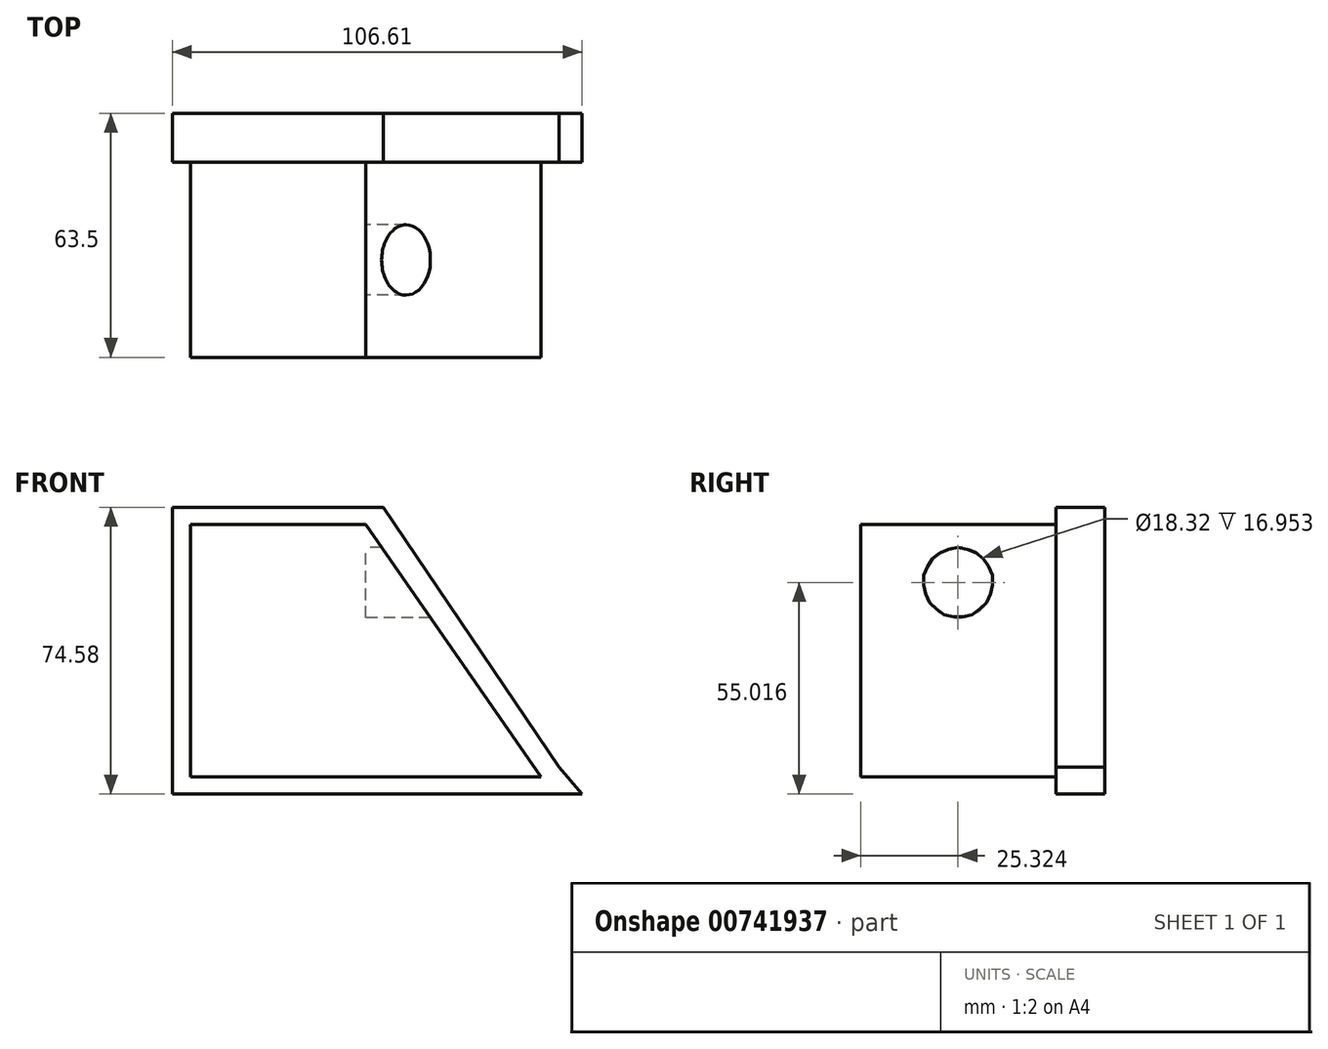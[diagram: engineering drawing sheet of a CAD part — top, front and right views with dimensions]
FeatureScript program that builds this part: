
annotation { "Feature Type Name" : "Feature", "Feature Type Description" : "" }
export const myFeature = defineFeature(function(context is Context, id is Id, definition is map)
    precondition{}
    {
        {
            var Q0;
            Q0=qCreatedBy(makeId("Front.planeOp"),FACE);
            var sketch = newSketch(context, id + "F0", { "sketchPlane" : qUnion([Q0])});
            skLineSegment(sketch, "E0.bottom", {"start": v(45.65, -32.81) * mm, "end": v(-45.65, -32.81) * mm});
            skLineSegment(sketch, "E0.top", {"start": v(0, 32.81) * mm, "end": v(-45.65, 32.81) * mm});
            skLineSegment(sketch, "E0.right", {"start": v(-45.65, -32.81) * mm, "end": v(-45.65, 32.81) * mm});
            skPoint(sketch, "E0.middle", {"position": v(0, 0) * mm});
            skLineSegment(sketch, "E1", {"start": v(45.65, -32.81) * mm, "end": v(0, 32.81) * mm});
            skPoint(sketch, "E0.left.end.orphan", {"position": v(45.65, 32.81) * mm});
            skSolve(sketch);
        }
        {
            var Q0;
            Q0=qCreatedBy(makeId("Front.planeOp"),FACE);
            var sketch = newSketch(context, id + "F1", { "sketchPlane" : qUnion([Q0])});
            skLineSegment(sketch, "E2.bottom", {"start": v(-50.31, 37.29) * mm, "end": v(4.53, 37.29) * mm});
            skLineSegment(sketch, "E2.top", {"start": v(-50.31, -37.29) * mm, "end": v(50.31, -37.29) * mm});
            skLineSegment(sketch, "E2.left", {"start": v(-50.31, 37.29) * mm, "end": v(-50.31, -37.29) * mm});
            skPoint(sketch, "E2.middle", {"position": v(0, 0) * mm});
            skLineSegment(sketch, "E3", {"start": v(50.31, -30.28) * mm, "end": v(4.53, 37.29) * mm});
            skPoint(sketch, "E4.orphan", {"position": v(50.31, 37.29) * mm});
            skLineSegment(sketch, "E5", {"start": v(50.31, -30.28) * mm, "end": v(56.3, -37.29) * mm});
            skLineSegment(sketch, "E6", {"start": v(56.3, -37.29) * mm, "end": v(50.31, -37.29) * mm});
            skSolve(sketch);
        }
        {
            var Q0;
            Q0=makeQuery(id+"F0.imprint","IMPRINT",FACE,{"disambiguationData":[TD([[makeQuery(id+"F0.imprint","IMPRINT",EDGE,{"derivedFrom":sQuery(id+"F0.wireOp",EDGE,"E0.bottom")}),-1.0]])]});
            extrude(context, id + "F2", {"entities" : qUnion([Q0]), "depth" : 50.8 * mm, "offsetDistance" : 25.4 * mm});
        }
        {
            var Q0;
            Q0 = qSketchRegion(id + "F1", true);
            extrude(context, id + "F3", {"entities" : qUnion([Q0]), "operationType" : NewBodyOperationType.ADD, "depth" : -12.7 * mm, "offsetDistance" : 25.4 * mm});
        }
        {
            var Q0;
            Q0=qCreatedBy(makeId("Right.planeOp"),FACE);
            var sketch = newSketch(context, id + "F4", { "sketchPlane" : qUnion([Q0])});
            skCircle(sketch, "E7", {"center": v(-25.48, 17.73) * mm, "radius": 9.16 * mm});
            skSolve(sketch);
        }
        {
            var Q0;
            Q0 = qSketchRegion(id + "F4", true);
            extrude(context, id + "F5", {"entities" : qUnion([Q0]), "operationType" : NewBodyOperationType.REMOVE, "depth" : 50.8 * mm, "offsetDistance" : 25.4 * mm});
        }
    });
